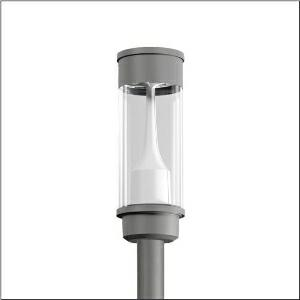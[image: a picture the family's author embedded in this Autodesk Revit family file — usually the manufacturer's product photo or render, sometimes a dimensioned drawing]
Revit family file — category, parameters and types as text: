
# Revit family: litepole_iq___st1_2a_5xa5415ef14h_6754
name_source: partatom
category: Lighting Fixtures
units: mm (PartAtom-declared; Revit-internal decimal feet)

## family parameters
Cut with Voids When Loaded = No
Host = Face
Light Source = No
Part Type = Normal
Room Calculation Point = No
Round Connector Dimension = Use Diameter
Shared = No

## types (1)
- --- (1 x LED, 1540 lm, 10.5 W, 3000K)
    Apparent Load = 11 VA
    CIE Flux Codes = 22 61 93 96 100
    Color Rendering = 70
    Color Temperature = 3000K
    Default Elevation = 1800 mm
    Description = Litepole iQ, mast luminaire, Module 540 iQ-SR, primary light control with 3 zone facetted reflector, of plastic, silver coated, highly specular, structured, primary optical cover: cover, of PMMA, transparent, light distribution: ST1.2a, light emission: direct distribution, primary light characteristic: asymmetric, installation type: post-top, LED, High Power LED, rated luminous flux: 1.540lm, luminous efficacy: 147lm/W, light colour: 730, colour temperature: 3000K, control gear: ECG iQ, control: Auto-Match, Temp-Guard, Lumen-Switch, Night-Set, Smart-Wire, Light-Fading, Desk-Remote (wireless, voltage-free reading and setting of iQ features in the workshop via application-optimized NFC function/RFID function), optimised constant luminous flux control (CLO 2.0), Street-Remote, presetting dimming logarithmic, with terminal, 6-pole, max. 2.5mm², mains connection: 220..240V, AC, 50/60Hz, start of lifetime: 11W, end of lifetime: 11W, reduction: 5W, luminaire housing, upper part, of glass-fibre reinforced polyester, coated, Siteco® metallic grey (DB 702S), diameter: 210mm, height: 590mm, spigot size: d x l = 76 x 70mm (post-top) | with reducer (optional accessory) 60 x 70mm, post-top mast mounting element, of diecast aluminium, coated, Siteco® metallic grey (DB 702S), Module 540 iQ-SR, traffic white (RAL 9016), equipment: standard, protection rating (complete): IP65, insulation class (complete): insulation class II (safety insulation), certification: CE, ENEC, VDE, packaging unit: 1 piece

Light Distribution: ST1.2a
    Height = 590 mm
    Lamp = 1 x LED
    Lamp Light Flux = 1540 lm
    Lamp Power = 10.5 W
    Lamp count = 1
    Length = 220 mm
    Luminous efficacy = 147 lm/W
    Manufacturer = Siteco
    ModVariant = No
    Model = 5XA5415EF14H
    Number of Poles = 1
    OnlyDefault = Yes
    Power Factor = 1
    Product Name = Litepole iQ | ST1.2a
    Product group = mast luminaire | pylon top
    ProductGroupID = 6100
    Protection Class = Protection class II
    Protection Degree = IP 65
    RLX_Detail_Level = 1
    RlxData = <blob elided: 71777 chars, md5=1c0250ea>
    Socket = socket
    Standby Power = 0 W
    System Light Flux = 1540 lm
    System Power = 11 W
    Type Comments = factory setting: luminous flux: 100 % | dim-lin: 254 | 419 mA
    Type Image = l_1006025.jpg
    URL = http://relux.com
    VarID = @adj_070105
    Voltage = 0 V
    Weight = 0.00 kg
    Width = 0 mm  [stored 0 ft]

note: [stored X ft] marks values corroborated as IEEE doubles in the binary element streams (Revit-internal decimal feet)

## geometry (parser evidence)
native form markers: Blend x4, Sweep x9
no freeform markers — native parametric forms only
